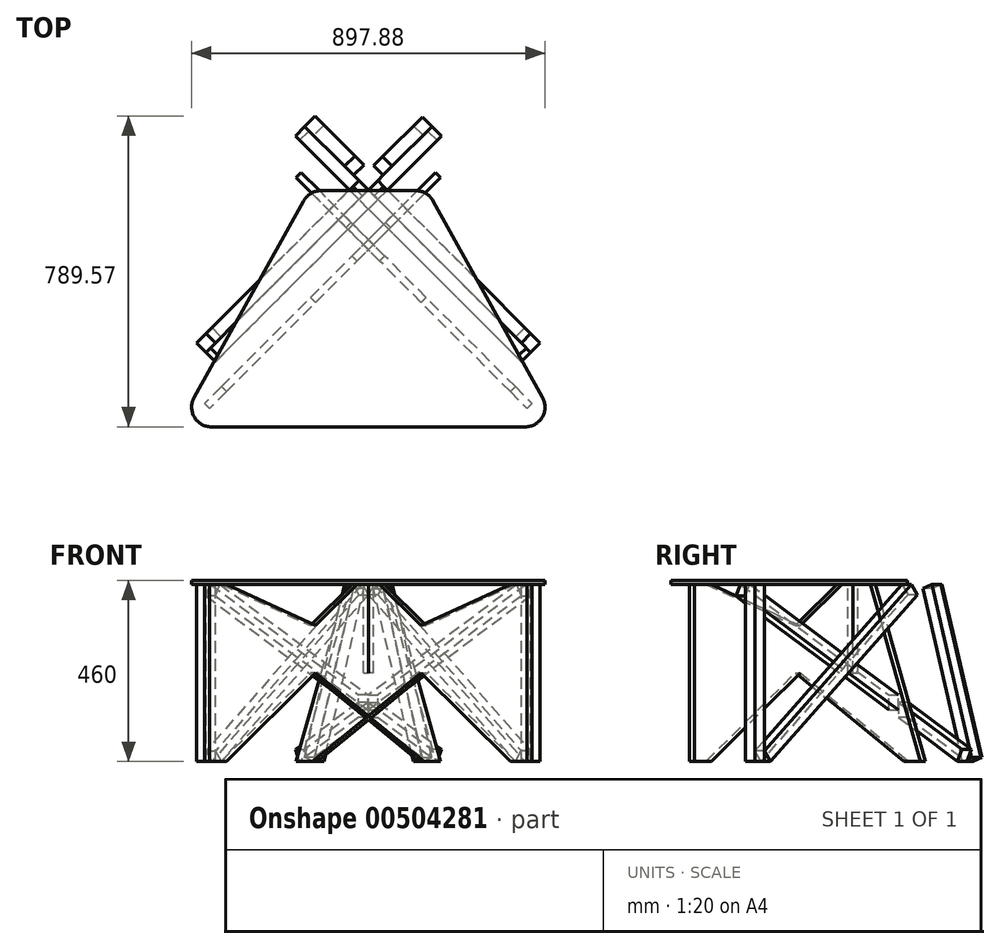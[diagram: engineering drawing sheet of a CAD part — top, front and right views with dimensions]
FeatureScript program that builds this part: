
annotation { "Feature Type Name" : "Feature", "Feature Type Description" : "" }
export const myFeature = defineFeature(function(context is Context, id is Id, definition is map)
    precondition{}
    {
        {
            var Q0;
            Q0=qCreatedBy(makeId("Top.planeOp"),FACE);
            var sketch = newSketch(context, id + "F0", { "sketchPlane" : qUnion([Q0])});
            skLineSegment(sketch, "E0.bottom", {"start": v(450, -300) * mm, "end": v(-450, -300) * mm, "construction": true});
            skLineSegment(sketch, "E0.top", {"start": v(450, 300) * mm, "end": v(-450, 300) * mm, "construction": true});
            skLineSegment(sketch, "E0.left", {"start": v(450, -300) * mm, "end": v(450, 300) * mm, "construction": true});
            skLineSegment(sketch, "E0.right", {"start": v(-450, -300) * mm, "end": v(-450, 300) * mm, "construction": true});
            skPoint(sketch, "E0.middle", {"position": v(0, 0) * mm});
            skLineSegment(sketch, "E1", {"start": v(-450, -250) * mm, "end": v(100, 300) * mm, "construction": true});
            skPoint(sketch, "E2", {"position": v(0, 300) * mm});
            skLineSegment(sketch, "E3.0", {"start": v(-425.96, -274.04) * mm, "end": v(148.08, 300) * mm, "construction": true});
            skLineSegment(sketch, "E4.0", {"start": v(-401.92, -298.08) * mm, "end": v(196.17, 300) * mm, "construction": true});
            skLineSegment(sketch, "E5.MirrorCS", {"start": v(401.92, -298.08) * mm, "end": v(-196.17, 300) * mm, "construction": true});
            skLineSegment(sketch, "E6.MirrorCS", {"start": v(450, -250) * mm, "end": v(-100, 300) * mm, "construction": true});
            skLineSegment(sketch, "E7.MirrorCS", {"start": v(425.96, -274.04) * mm, "end": v(-148.08, 300) * mm, "construction": true});
            skLineSegment(sketch, "E8", {"start": v(-24.04, 127.88) * mm, "end": v(0, 103.83) * mm});
            skLineSegment(sketch, "E9", {"start": v(0, 200) * mm, "end": v(24.04, 175.96) * mm});
            skLineSegment(sketch, "E10", {"start": v(-24.75, 127.88) * mm, "end": v(0, 152.62) * mm});
            skLineSegment(sketch, "E11", {"start": v(0, 152.62) * mm, "end": v(24.75, 127.88) * mm});
            skLineSegment(sketch, "E12", {"start": v(24.75, 127.88) * mm, "end": v(0, 103.13) * mm});
            skLineSegment(sketch, "E13", {"start": v(0, 103.13) * mm, "end": v(-24.75, 127.88) * mm});
            skLineSegment(sketch, "E14", {"start": v(-24.04, 127.88) * mm, "end": v(24.04, 127.88) * mm, "construction": true});
            skLineSegment(sketch, "E15", {"start": v(-164.3, 274.32) * mm, "end": v(-442.63, -225.68) * mm});
            skLineSegment(sketch, "E16", {"start": v(-398.94, -300) * mm, "end": v(398.94, -300) * mm});
            skLineSegment(sketch, "E17", {"start": v(442.63, -225.68) * mm, "end": v(164.3, 274.32) * mm});
            skLineSegment(sketch, "E18", {"start": v(120.6, 300) * mm, "end": v(-120.6, 300) * mm});
            skPoint(sketch, "E19.visualSharp", {"position": v(-484, -300) * mm});
            skArc(sketch, "E19.filletArc", {"start": v(-442.63, -225.68) * mm, "mid": v(-442.05, -275.34) * mm, "end": v(-398.94, -300) * mm});
            skPoint(sketch, "E20.visualSharp", {"position": v(484, -300) * mm});
            skArc(sketch, "E20.filletArc", {"start": v(398.94, -300) * mm, "mid": v(442.05, -275.34) * mm, "end": v(442.63, -225.68) * mm});
            skPoint(sketch, "E21.visualSharp", {"position": v(150, 300) * mm});
            skArc(sketch, "E21.filletArc", {"start": v(164.3, 274.32) * mm, "mid": v(145.95, 293.1) * mm, "end": v(120.6, 300) * mm});
            skPoint(sketch, "E22.visualSharp", {"position": v(-150, 300) * mm});
            skArc(sketch, "E22.filletArc", {"start": v(-120.6, 300) * mm, "mid": v(-145.95, 293.1) * mm, "end": v(-164.3, 274.32) * mm});
            skSolve(sketch);
        }
        {
            var Q0;
            Q0=qCreatedBy(makeId("Right.planeOp"),FACE);
            var sketch = newSketch(context, id + "F1", { "sketchPlane" : qUnion([Q0])});
            skLineSegment(sketch, "E23.bottom", {"start": v(405.9, -225) * mm, "end": v(-405.9, -225) * mm});
            skLineSegment(sketch, "E23.top", {"start": v(405.9, 225) * mm, "end": v(-405.9, 225) * mm});
            skLineSegment(sketch, "E23.left", {"start": v(405.9, -225) * mm, "end": v(405.9, 225) * mm});
            skLineSegment(sketch, "E23.right", {"start": v(-405.91, -225) * mm, "end": v(-405.91, 225) * mm});
            skPoint(sketch, "E23.middle", {"position": v(0, 0) * mm});
            skLineSegment(sketch, "E24.0", {"start": v(-371.91, -225) * mm, "end": v(-371.91, 225) * mm});
            skLineSegment(sketch, "E25", {"start": v(-390.04, 225) * mm, "end": v(405.91, -194.93) * mm});
            skLineSegment(sketch, "E26.0", {"start": v(-405.91, 194.93) * mm, "end": v(390.04, -225) * mm});
            skLineSegment(sketch, "E27", {"start": v(-405.91, 194.93) * mm, "end": v(-390.04, 225) * mm});
            skLineSegment(sketch, "E28", {"start": v(390.04, -225) * mm, "end": v(405.9, -194.93) * mm});
            skLineSegment(sketch, "E29", {"start": v(-397.98, 209.96) * mm, "end": v(397.98, -209.96) * mm, "construction": true});
            skLineSegment(sketch, "E30", {"start": v(-405.9, -85.73) * mm, "end": v(162.5, -85.73) * mm, "construction": true});
            skLineSegment(sketch, "E31", {"start": v(162.5, -85.73) * mm, "end": v(170.42, -70.7) * mm});
            skLineSegment(sketch, "E32", {"start": v(162.5, -85.73) * mm, "end": v(154.56, -100.76) * mm});
            skLineSegment(sketch, "E33", {"start": v(162.49, -85.73) * mm, "end": v(192.56, -101.6) * mm});
            skLineSegment(sketch, "E34", {"start": v(192.56, -101.6) * mm, "end": v(200.5, -86.56) * mm});
            skLineSegment(sketch, "E35", {"start": v(192.56, -101.6) * mm, "end": v(184.63, -116.63) * mm});
            skLineSegment(sketch, "E36", {"start": v(177.53, -93.66) * mm, "end": v(177.53, 225) * mm, "construction": true});
            skLineSegment(sketch, "E37", {"start": v(405.9, -214.47) * mm, "end": v(262.82, 225) * mm});
            skLineSegment(sketch, "E38.0", {"start": v(373.58, -225) * mm, "end": v(230.49, 214.47) * mm});
            skLineSegment(sketch, "E39", {"start": v(262.82, 225) * mm, "end": v(230.49, 214.47) * mm});
            skLineSegment(sketch, "E40", {"start": v(373.58, -225) * mm, "end": v(405.9, -214.47) * mm});
            skLineSegment(sketch, "E41", {"start": v(156.26, 225) * mm, "end": v(-371.9, -198.47) * mm});
            skLineSegment(sketch, "E42.0", {"start": v(177.53, 198.47) * mm, "end": v(-350.64, -225) * mm});
            skLineSegment(sketch, "E43", {"start": v(156.26, 225) * mm, "end": v(177.53, 198.47) * mm});
            skLineSegment(sketch, "E44", {"start": v(-350.64, -225) * mm, "end": v(-371.9, -198.47) * mm});
            skLineSegment(sketch, "E45", {"start": v(177.53, -74.44) * mm, "end": v(135, -52) * mm});
            skLineSegment(sketch, "E46", {"start": v(135, -52) * mm, "end": v(135, -90.44) * mm});
            skLineSegment(sketch, "E47", {"start": v(135, -71.22) * mm, "end": v(162.5, -85.73) * mm});
            skLineSegment(sketch, "E48", {"start": v(177.53, -74.44) * mm, "end": v(177.53, -93.66) * mm});
            skSolve(sketch);
        }
        {
            var Q0;
            {var subQ4=sQuery(id+"F1.wireOp",EDGE,"E23.right");var subQ6=sQuery(id+"F1.wireOp",EDGE,"E23.bottom");var subQ8=makeQuery(id+"F1.imprint","INTERSECT",VERTEX,{"derivedFrom":[subQ6,subQ4]});Q0=makeQuery(id+"F1.imprint","IMPRINT",FACE,{"disambiguationData":[TD([[makeQuery(id+"F1.imprint","IMPRINT",EDGE,{"disambiguationData":[TD([[subQ8,1.0]])],"derivedFrom":subQ6}),-1.0]])]});}
            var Q1;
            {var subQ5=sQuery(id+"F1.wireOp",EDGE,"E27");Q1=makeQuery(id+"F1.imprint","IMPRINT",FACE,{"disambiguationData":[TD([[makeQuery(id+"F1.imprint","IMPRINT",EDGE,{"derivedFrom":subQ5}),-1.0]])]});}
            var Q2;
            {var subQ0=sQuery(id+"F1.wireOp",EDGE,"E24.0");var subQ1=sQuery(id+"F1.wireOp",EDGE,"E23.top");var subQ2=makeQuery(id+"F1.imprint","INTERSECT",VERTEX,{"derivedFrom":[subQ1,subQ0]});Q2=makeQuery(id+"F1.imprint","IMPRINT",FACE,{"disambiguationData":[TD([[makeQuery(id+"F1.imprint","IMPRINT",EDGE,{"disambiguationData":[TD([[subQ2,1.0]])],"derivedFrom":subQ0}),1.0]])]});}
            var Q3;
            {var subQ3=sQuery(id+"F1.wireOp",EDGE,"E27");Q3=makeQuery(id+"F1.imprint","IMPRINT",FACE,{"disambiguationData":[TD([[makeQuery(id+"F1.imprint","IMPRINT",EDGE,{"derivedFrom":subQ3}),1.0]])]});}
            extrude(context, id + "F2", {"entities" : qUnion([Q0, Q1, Q2, Q3]), "depth" : 34 * mm});
        }
        {
            var Q0;
            {var subQ5=sQuery(id+"F1.wireOp",EDGE,"E44");Q0=makeQuery(id+"F1.imprint","IMPRINT",FACE,{"disambiguationData":[TD([[makeQuery(id+"F1.imprint","IMPRINT",EDGE,{"derivedFrom":subQ5}),-1.0]])]});}
            var Q1;
            {var subQ0=sQuery(id+"F1.wireOp",EDGE,"E41");var subQ1=sQuery(id+"F1.wireOp",EDGE,"E25");var subQ2=makeQuery(id+"F1.imprint","INTERSECT",VERTEX,{"derivedFrom":[subQ1,subQ0]});Q1=makeQuery(id+"F1.imprint","IMPRINT",FACE,{"disambiguationData":[TD([[makeQuery(id+"F1.imprint","IMPRINT",EDGE,{"disambiguationData":[TD([[subQ2,-1.0]])],"derivedFrom":subQ1}),-1.0]])]});}
            var Q2;
            {var subQ5=sQuery(id+"F1.wireOp",EDGE,"E43");Q2=makeQuery(id+"F1.imprint","IMPRINT",FACE,{"disambiguationData":[TD([[makeQuery(id+"F1.imprint","IMPRINT",EDGE,{"derivedFrom":subQ5}),-1.0]])]});}
            extrude(context, id + "F3", {"entities" : qUnion([Q0, Q1, Q2]), "depth" : 34 * mm});
        }
        {
            var Q0;
            {var subQ5=sQuery(id+"F1.wireOp",EDGE,"E27");Q0=makeQuery(id+"F1.imprint","IMPRINT",FACE,{"disambiguationData":[TD([[makeQuery(id+"F1.imprint","IMPRINT",EDGE,{"derivedFrom":subQ5}),-1.0]])]});}
            var Q1;
            {var subQ0=sQuery(id+"F1.wireOp",EDGE,"E26.0");var subQ1=sQuery(id+"F1.wireOp",EDGE,"E24.0");var subQ2=makeQuery(id+"F1.imprint","INTERSECT",VERTEX,{"derivedFrom":[subQ1,subQ0]});Q1=makeQuery(id+"F1.imprint","IMPRINT",FACE,{"disambiguationData":[TD([[makeQuery(id+"F1.imprint","IMPRINT",EDGE,{"disambiguationData":[TD([[subQ2,-1.0]])],"derivedFrom":subQ1}),-1.0]])]});}
            var Q2;
            {var subQ0=sQuery(id+"F1.wireOp",EDGE,"E41");var subQ1=sQuery(id+"F1.wireOp",EDGE,"E25");var subQ2=makeQuery(id+"F1.imprint","INTERSECT",VERTEX,{"derivedFrom":[subQ1,subQ0]});Q2=makeQuery(id+"F1.imprint","IMPRINT",FACE,{"disambiguationData":[TD([[makeQuery(id+"F1.imprint","IMPRINT",EDGE,{"disambiguationData":[TD([[subQ2,-1.0]])],"derivedFrom":subQ1}),-1.0]])]});}
            var Q3;
            {var subQ0=sQuery(id+"F1.wireOp",EDGE,"E32");Q3=makeQuery(id+"F1.imprint","IMPRINT",FACE,{"disambiguationData":[TD([[makeQuery(id+"F1.imprint","IMPRINT",EDGE,{"derivedFrom":subQ0}),1.0]])]});}
            var Q4;
            {var subQ4=sQuery(id+"F1.wireOp",EDGE,"E34");Q4=makeQuery(id+"F1.imprint","IMPRINT",FACE,{"disambiguationData":[TD([[makeQuery(id+"F1.imprint","IMPRINT",EDGE,{"derivedFrom":subQ4}),-1.0]])]});}
            var Q5;
            {var subQ5=sQuery(id+"F1.wireOp",EDGE,"E38.0");var subQ6=sQuery(id+"F1.wireOp",EDGE,"E25");var subQ7=makeQuery(id+"F1.imprint","INTERSECT",VERTEX,{"derivedFrom":[subQ6,subQ5]});Q5=makeQuery(id+"F1.imprint","IMPRINT",FACE,{"disambiguationData":[TD([[makeQuery(id+"F1.imprint","IMPRINT",EDGE,{"disambiguationData":[TD([[subQ7,-1.0]])],"derivedFrom":subQ6}),-1.0]])]});}
            var Q6;
            {var subQ1=sQuery(id+"F1.wireOp",EDGE,"E26.0");var subQ3=sQuery(id+"F1.wireOp",EDGE,"E40");var subQ4=makeQuery(id+"F1.imprint","INTERSECT",VERTEX,{"derivedFrom":[subQ1,subQ3]});Q6=makeQuery(id+"F1.imprint","IMPRINT",FACE,{"disambiguationData":[TD([[makeQuery(id+"F1.imprint","IMPRINT",EDGE,{"disambiguationData":[TD([[subQ4,-1.0]])],"derivedFrom":subQ3}),-1.0]])]});}
            var Q7;
            {var subQ1=sQuery(id+"F1.wireOp",EDGE,"E25");var subQ3=sQuery(id+"F1.wireOp",EDGE,"E37");var subQ4=makeQuery(id+"F1.imprint","INTERSECT",VERTEX,{"derivedFrom":[subQ1,subQ3]});Q7=makeQuery(id+"F1.imprint","IMPRINT",FACE,{"disambiguationData":[TD([[makeQuery(id+"F1.imprint","IMPRINT",EDGE,{"disambiguationData":[TD([[subQ4,1.0]])],"derivedFrom":subQ3}),-1.0]])]});}
            var Q8;
            {var subQ0=sQuery(id+"F1.wireOp",EDGE,"E34");Q8=makeQuery(id+"F1.imprint","IMPRINT",FACE,{"disambiguationData":[TD([[makeQuery(id+"F1.imprint","IMPRINT",EDGE,{"derivedFrom":subQ0}),1.0]])]});}
            var Q9;
            {var subQ0=sQuery(id+"F1.wireOp",EDGE,"E32");Q9=makeQuery(id+"F1.imprint","IMPRINT",FACE,{"disambiguationData":[TD([[makeQuery(id+"F1.imprint","IMPRINT",EDGE,{"derivedFrom":subQ0}),-1.0]])]});}
            var Q10;
            {var subQ0=sQuery(id+"F1.wireOp",EDGE,"E46");var subQ6=sQuery(id+"F1.wireOp",EDGE,"E26.0");var subQ8=makeQuery(id+"F1.imprint","INTERSECT",VERTEX,{"derivedFrom":[subQ6,subQ0]});Q10=makeQuery(id+"F1.imprint","IMPRINT",FACE,{"disambiguationData":[TD([[makeQuery(id+"F1.imprint","IMPRINT",EDGE,{"disambiguationData":[TD([[subQ8,1.0]])],"derivedFrom":subQ6}),1.0]])]});}
            var Q11;
            {var subQ0=sQuery(id+"F1.wireOp",EDGE,"E31");Q11=makeQuery(id+"F1.imprint","IMPRINT",FACE,{"disambiguationData":[TD([[makeQuery(id+"F1.imprint","IMPRINT",EDGE,{"derivedFrom":subQ0}),-1.0]])]});}
            var Q12;
            {var subQ0=sQuery(id+"F1.wireOp",EDGE,"E31");Q12=makeQuery(id+"F1.imprint","IMPRINT",FACE,{"disambiguationData":[TD([[makeQuery(id+"F1.imprint","IMPRINT",EDGE,{"derivedFrom":subQ0}),1.0]])]});}
            extrude(context, id + "F4", {"entities" : qUnion([Q0, Q1, Q2, Q3, Q4, Q5, Q6, Q7, Q8, Q9, Q10, Q11, Q12]), "oppositeDirection" : true, "depth" : 34 * mm});
        }
        {
            var Q0;
            {var subQ5=sQuery(id+"F1.wireOp",EDGE,"E39");Q0=makeQuery(id+"F1.imprint","IMPRINT",FACE,{"disambiguationData":[TD([[makeQuery(id+"F1.imprint","IMPRINT",EDGE,{"derivedFrom":subQ5}),1.0]])]});}
            var Q1;
            {var subQ5=sQuery(id+"F1.wireOp",EDGE,"E38.0");var subQ6=sQuery(id+"F1.wireOp",EDGE,"E25");var subQ7=makeQuery(id+"F1.imprint","INTERSECT",VERTEX,{"derivedFrom":[subQ6,subQ5]});Q1=makeQuery(id+"F1.imprint","IMPRINT",FACE,{"disambiguationData":[TD([[makeQuery(id+"F1.imprint","IMPRINT",EDGE,{"disambiguationData":[TD([[subQ7,-1.0]])],"derivedFrom":subQ6}),-1.0]])]});}
            var Q2;
            {var subQ0=sQuery(id+"F1.wireOp",EDGE,"E40");var subQ1=sQuery(id+"F1.wireOp",EDGE,"E28");var subQ2=makeQuery(id+"F1.imprint","INTERSECT",VERTEX,{"derivedFrom":[subQ1,subQ0]});Q2=makeQuery(id+"F1.imprint","IMPRINT",FACE,{"disambiguationData":[TD([[makeQuery(id+"F1.imprint","IMPRINT",EDGE,{"disambiguationData":[TD([[subQ2,-1.0]])],"derivedFrom":subQ1}),-1.0]])]});}
            var Q3;
            {var subQ0=sQuery(id+"F1.wireOp",EDGE,"E38.0");var subQ1=sQuery(id+"F1.wireOp",EDGE,"E26.0");var subQ2=makeQuery(id+"F1.imprint","INTERSECT",VERTEX,{"derivedFrom":[subQ1,subQ0]});Q3=makeQuery(id+"F1.imprint","IMPRINT",FACE,{"disambiguationData":[TD([[makeQuery(id+"F1.imprint","IMPRINT",EDGE,{"disambiguationData":[TD([[subQ2,-1.0]])],"derivedFrom":subQ1}),-1.0]])]});}
            extrude(context, id + "F5", {"entities" : qUnion([Q0, Q1, Q2, Q3]), "depth" : 37 * mm});
        }
        {
            var Q0;
            Q0=makeQuery(id+"F2.opExtrude","SWEPT_BODY",BODY,{"disambiguationData":[OSD([sQuery(id+"F1.wireOp",EDGE,"E23.bottom"),sQuery(id+"F1.wireOp",EDGE,"E23.top"),sQuery(id+"F1.wireOp",EDGE,"E23.right"),sQuery(id+"F1.wireOp",EDGE,"E24.0")])]});
            var Q1;
            Q1=makeQuery(id+"F3.opExtrude","SWEPT_BODY",BODY,{"disambiguationData":[OSD([sQuery(id+"F1.wireOp",EDGE,"E41"),sQuery(id+"F1.wireOp",EDGE,"E42.0"),sQuery(id+"F1.wireOp",EDGE,"E43"),sQuery(id+"F1.wireOp",EDGE,"E44")])]});
            var Q2;
            Q2=makeQuery(id+"F4.opExtrude","SWEPT_BODY",BODY,{"disambiguationData":[OSD([sQuery(id+"F1.wireOp",EDGE,"E25"),sQuery(id+"F1.wireOp",EDGE,"E26.0"),sQuery(id+"F1.wireOp",EDGE,"E27"),sQuery(id+"F1.wireOp",EDGE,"E28"),sQuery(id+"F1.wireOp",EDGE,"E31"),sQuery(id+"F1.wireOp",EDGE,"E33"),sQuery(id+"F1.wireOp",EDGE,"E34")])]});
            var Q3;
            Q3=makeQuery(id+"F5.opExtrude","SWEPT_BODY",BODY,{"disambiguationData":[OSD([sQuery(id+"F1.wireOp",EDGE,"E37"),sQuery(id+"F1.wireOp",EDGE,"E38.0"),sQuery(id+"F1.wireOp",EDGE,"E39"),sQuery(id+"F1.wireOp",EDGE,"E40")])]});
            var Q4;
            Q4=sQuery(id+"F1.wireOp",EDGE,"E36");
            transform(context, id + "F6", {"entities" : qUnion([Q0, Q1, Q2, Q3]), "transformType" : TransformType.ROTATION, "transformAxis" : qUnion([Q4]), "angle" : 45 * degree, "makeCopy" : false});
        }
        {
            var Q0;
            {var subQ0=sQuery(id+"F1.wireOp",EDGE,"E41");var subQ1=sQuery(id+"F1.wireOp",EDGE,"E25");var subQ2=makeQuery(id+"F1.imprint","INTERSECT",VERTEX,{"derivedFrom":[subQ1,subQ0]});Q0=makeQuery(id+"F1.imprint","IMPRINT",FACE,{"disambiguationData":[TD([[makeQuery(id+"F1.imprint","IMPRINT",EDGE,{"disambiguationData":[TD([[subQ2,-1.0]])],"derivedFrom":subQ1}),-1.0]])]});}
            var Q1;
            {var subQ0=sQuery(id+"F1.wireOp",EDGE,"E26.0");var subQ1=sQuery(id+"F1.wireOp",EDGE,"E24.0");var subQ2=makeQuery(id+"F1.imprint","INTERSECT",VERTEX,{"derivedFrom":[subQ1,subQ0]});Q1=makeQuery(id+"F1.imprint","IMPRINT",FACE,{"disambiguationData":[TD([[makeQuery(id+"F1.imprint","IMPRINT",EDGE,{"disambiguationData":[TD([[subQ2,-1.0]])],"derivedFrom":subQ1}),-1.0]])]});}
            var Q2;
            {var subQ4=sQuery(id+"F1.wireOp",EDGE,"E34");Q2=makeQuery(id+"F1.imprint","IMPRINT",FACE,{"disambiguationData":[TD([[makeQuery(id+"F1.imprint","IMPRINT",EDGE,{"derivedFrom":subQ4}),-1.0]])]});}
            var Q3;
            {var subQ5=sQuery(id+"F1.wireOp",EDGE,"E38.0");var subQ6=sQuery(id+"F1.wireOp",EDGE,"E25");var subQ7=makeQuery(id+"F1.imprint","INTERSECT",VERTEX,{"derivedFrom":[subQ6,subQ5]});Q3=makeQuery(id+"F1.imprint","IMPRINT",FACE,{"disambiguationData":[TD([[makeQuery(id+"F1.imprint","IMPRINT",EDGE,{"disambiguationData":[TD([[subQ7,-1.0]])],"derivedFrom":subQ6}),-1.0]])]});}
            var Q4;
            {var subQ5=sQuery(id+"F1.wireOp",EDGE,"E27");Q4=makeQuery(id+"F1.imprint","IMPRINT",FACE,{"disambiguationData":[TD([[makeQuery(id+"F1.imprint","IMPRINT",EDGE,{"derivedFrom":subQ5}),-1.0]])]});}
            var Q5;
            {var subQ1=sQuery(id+"F1.wireOp",EDGE,"E25");var subQ3=sQuery(id+"F1.wireOp",EDGE,"E37");var subQ4=makeQuery(id+"F1.imprint","INTERSECT",VERTEX,{"derivedFrom":[subQ1,subQ3]});Q5=makeQuery(id+"F1.imprint","IMPRINT",FACE,{"disambiguationData":[TD([[makeQuery(id+"F1.imprint","IMPRINT",EDGE,{"disambiguationData":[TD([[subQ4,1.0]])],"derivedFrom":subQ3}),-1.0]])]});}
            var Q6;
            {var subQ1=sQuery(id+"F1.wireOp",EDGE,"E26.0");var subQ3=sQuery(id+"F1.wireOp",EDGE,"E40");var subQ4=makeQuery(id+"F1.imprint","INTERSECT",VERTEX,{"derivedFrom":[subQ1,subQ3]});Q6=makeQuery(id+"F1.imprint","IMPRINT",FACE,{"disambiguationData":[TD([[makeQuery(id+"F1.imprint","IMPRINT",EDGE,{"disambiguationData":[TD([[subQ4,-1.0]])],"derivedFrom":subQ3}),-1.0]])]});}
            var Q7;
            {var subQ0=sQuery(id+"F1.wireOp",EDGE,"E46");var subQ6=sQuery(id+"F1.wireOp",EDGE,"E26.0");var subQ8=makeQuery(id+"F1.imprint","INTERSECT",VERTEX,{"derivedFrom":[subQ6,subQ0]});Q7=makeQuery(id+"F1.imprint","IMPRINT",FACE,{"disambiguationData":[TD([[makeQuery(id+"F1.imprint","IMPRINT",EDGE,{"disambiguationData":[TD([[subQ8,1.0]])],"derivedFrom":subQ6}),1.0]])]});}
            var Q8;
            {var subQ0=sQuery(id+"F1.wireOp",EDGE,"E34");Q8=makeQuery(id+"F1.imprint","IMPRINT",FACE,{"disambiguationData":[TD([[makeQuery(id+"F1.imprint","IMPRINT",EDGE,{"derivedFrom":subQ0}),1.0]])]});}
            var Q9;
            {var subQ0=sQuery(id+"F1.wireOp",EDGE,"E31");Q9=makeQuery(id+"F1.imprint","IMPRINT",FACE,{"disambiguationData":[TD([[makeQuery(id+"F1.imprint","IMPRINT",EDGE,{"derivedFrom":subQ0}),1.0]])]});}
            var Q10;
            {var subQ0=sQuery(id+"F1.wireOp",EDGE,"E31");Q10=makeQuery(id+"F1.imprint","IMPRINT",FACE,{"disambiguationData":[TD([[makeQuery(id+"F1.imprint","IMPRINT",EDGE,{"derivedFrom":subQ0}),-1.0]])]});}
            var Q11;
            {var subQ3=sQuery(id+"F1.wireOp",EDGE,"E32");Q11=makeQuery(id+"F1.imprint","IMPRINT",FACE,{"disambiguationData":[TD([[makeQuery(id+"F1.imprint","IMPRINT",EDGE,{"derivedFrom":subQ3}),1.0]])]});}
            var Q12;
            {var subQ0=sQuery(id+"F1.wireOp",EDGE,"E32");Q12=makeQuery(id+"F1.imprint","IMPRINT",FACE,{"disambiguationData":[TD([[makeQuery(id+"F1.imprint","IMPRINT",EDGE,{"derivedFrom":subQ0}),-1.0]])]});}
            extrude(context, id + "F7", {"entities" : qUnion([Q0, Q1, Q2, Q3, Q4, Q5, Q6, Q7, Q8, Q9, Q10, Q11, Q12]), "depth" : 34 * mm});
        }
        {
            var Q0;
            {var subQ5=sQuery(id+"F1.wireOp",EDGE,"E44");Q0=makeQuery(id+"F1.imprint","IMPRINT",FACE,{"disambiguationData":[TD([[makeQuery(id+"F1.imprint","IMPRINT",EDGE,{"derivedFrom":subQ5}),-1.0]])]});}
            var Q1;
            {var subQ0=sQuery(id+"F1.wireOp",EDGE,"E41");var subQ1=sQuery(id+"F1.wireOp",EDGE,"E25");var subQ2=makeQuery(id+"F1.imprint","INTERSECT",VERTEX,{"derivedFrom":[subQ1,subQ0]});Q1=makeQuery(id+"F1.imprint","IMPRINT",FACE,{"disambiguationData":[TD([[makeQuery(id+"F1.imprint","IMPRINT",EDGE,{"disambiguationData":[TD([[subQ2,-1.0]])],"derivedFrom":subQ1}),-1.0]])]});}
            var Q2;
            {var subQ5=sQuery(id+"F1.wireOp",EDGE,"E43");Q2=makeQuery(id+"F1.imprint","IMPRINT",FACE,{"disambiguationData":[TD([[makeQuery(id+"F1.imprint","IMPRINT",EDGE,{"derivedFrom":subQ5}),-1.0]])]});}
            extrude(context, id + "F8", {"entities" : qUnion([Q0, Q1, Q2]), "oppositeDirection" : true, "depth" : 34 * mm});
        }
        {
            var Q0;
            {var subQ4=sQuery(id+"F1.wireOp",EDGE,"E23.right");var subQ6=sQuery(id+"F1.wireOp",EDGE,"E23.bottom");var subQ8=makeQuery(id+"F1.imprint","INTERSECT",VERTEX,{"derivedFrom":[subQ6,subQ4]});Q0=makeQuery(id+"F1.imprint","IMPRINT",FACE,{"disambiguationData":[TD([[makeQuery(id+"F1.imprint","IMPRINT",EDGE,{"disambiguationData":[TD([[subQ8,1.0]])],"derivedFrom":subQ6}),-1.0]])]});}
            var Q1;
            {var subQ5=sQuery(id+"F1.wireOp",EDGE,"E27");Q1=makeQuery(id+"F1.imprint","IMPRINT",FACE,{"disambiguationData":[TD([[makeQuery(id+"F1.imprint","IMPRINT",EDGE,{"derivedFrom":subQ5}),-1.0]])]});}
            var Q2;
            {var subQ3=sQuery(id+"F1.wireOp",EDGE,"E27");Q2=makeQuery(id+"F1.imprint","IMPRINT",FACE,{"disambiguationData":[TD([[makeQuery(id+"F1.imprint","IMPRINT",EDGE,{"derivedFrom":subQ3}),1.0]])]});}
            var Q3;
            {var subQ0=sQuery(id+"F1.wireOp",EDGE,"E24.0");var subQ1=sQuery(id+"F1.wireOp",EDGE,"E23.top");var subQ2=makeQuery(id+"F1.imprint","INTERSECT",VERTEX,{"derivedFrom":[subQ1,subQ0]});Q3=makeQuery(id+"F1.imprint","IMPRINT",FACE,{"disambiguationData":[TD([[makeQuery(id+"F1.imprint","IMPRINT",EDGE,{"disambiguationData":[TD([[subQ2,1.0]])],"derivedFrom":subQ0}),1.0]])]});}
            extrude(context, id + "F9", {"entities" : qUnion([Q0, Q1, Q2, Q3]), "oppositeDirection" : true, "depth" : 34 * mm});
        }
        {
            var Q0;
            {var subQ5=sQuery(id+"F1.wireOp",EDGE,"E39");Q0=makeQuery(id+"F1.imprint","IMPRINT",FACE,{"disambiguationData":[TD([[makeQuery(id+"F1.imprint","IMPRINT",EDGE,{"derivedFrom":subQ5}),1.0]])]});}
            var Q1;
            {var subQ5=sQuery(id+"F1.wireOp",EDGE,"E38.0");var subQ6=sQuery(id+"F1.wireOp",EDGE,"E25");var subQ7=makeQuery(id+"F1.imprint","INTERSECT",VERTEX,{"derivedFrom":[subQ6,subQ5]});Q1=makeQuery(id+"F1.imprint","IMPRINT",FACE,{"disambiguationData":[TD([[makeQuery(id+"F1.imprint","IMPRINT",EDGE,{"disambiguationData":[TD([[subQ7,-1.0]])],"derivedFrom":subQ6}),-1.0]])]});}
            var Q2;
            {var subQ0=sQuery(id+"F1.wireOp",EDGE,"E40");var subQ1=sQuery(id+"F1.wireOp",EDGE,"E28");var subQ2=makeQuery(id+"F1.imprint","INTERSECT",VERTEX,{"derivedFrom":[subQ1,subQ0]});Q2=makeQuery(id+"F1.imprint","IMPRINT",FACE,{"disambiguationData":[TD([[makeQuery(id+"F1.imprint","IMPRINT",EDGE,{"disambiguationData":[TD([[subQ2,-1.0]])],"derivedFrom":subQ1}),-1.0]])]});}
            var Q3;
            {var subQ0=sQuery(id+"F1.wireOp",EDGE,"E38.0");var subQ1=sQuery(id+"F1.wireOp",EDGE,"E26.0");var subQ2=makeQuery(id+"F1.imprint","INTERSECT",VERTEX,{"derivedFrom":[subQ1,subQ0]});Q3=makeQuery(id+"F1.imprint","IMPRINT",FACE,{"disambiguationData":[TD([[makeQuery(id+"F1.imprint","IMPRINT",EDGE,{"disambiguationData":[TD([[subQ2,-1.0]])],"derivedFrom":subQ1}),-1.0]])]});}
            extrude(context, id + "F10", {"entities" : qUnion([Q0, Q1, Q2, Q3]), "oppositeDirection" : true, "depth" : 34 * mm});
        }
        {
            var Q0;
            Q0=makeQuery(id+"F7.opExtrude","SWEPT_BODY",BODY,{"disambiguationData":[OSD([sQuery(id+"F1.wireOp",EDGE,"E25"),sQuery(id+"F1.wireOp",EDGE,"E26.0"),sQuery(id+"F1.wireOp",EDGE,"E27"),sQuery(id+"F1.wireOp",EDGE,"E28"),sQuery(id+"F1.wireOp",EDGE,"E32"),sQuery(id+"F1.wireOp",EDGE,"E33"),sQuery(id+"F1.wireOp",EDGE,"E35")])]});
            var Q1;
            Q1=makeQuery(id+"F8.opExtrude","SWEPT_BODY",BODY,{"disambiguationData":[OSD([sQuery(id+"F1.wireOp",EDGE,"E41"),sQuery(id+"F1.wireOp",EDGE,"E42.0"),sQuery(id+"F1.wireOp",EDGE,"E43"),sQuery(id+"F1.wireOp",EDGE,"E44")])]});
            var Q2;
            Q2=makeQuery(id+"F9.opExtrude","SWEPT_BODY",BODY,{"disambiguationData":[OSD([sQuery(id+"F1.wireOp",EDGE,"E23.bottom"),sQuery(id+"F1.wireOp",EDGE,"E23.top"),sQuery(id+"F1.wireOp",EDGE,"E23.right"),sQuery(id+"F1.wireOp",EDGE,"E24.0")])]});
            var Q3;
            Q3=makeQuery(id+"F10.opExtrude","SWEPT_BODY",BODY,{"disambiguationData":[OSD([sQuery(id+"F1.wireOp",EDGE,"E37"),sQuery(id+"F1.wireOp",EDGE,"E38.0"),sQuery(id+"F1.wireOp",EDGE,"E39"),sQuery(id+"F1.wireOp",EDGE,"E40")])]});
            var Q4;
            Q4=sQuery(id+"F1.wireOp",EDGE,"E36");
            transform(context, id + "F11", {"entities" : qUnion([Q0, Q1, Q2, Q3]), "transformType" : TransformType.ROTATION, "transformAxis" : qUnion([Q4]), "angle" : 45 * degree, "oppositeDirection" : true, "makeCopy" : false});
        }
        {
            var Q0;
            Q0=makeQuery(id+"F2.opExtrude","SWEPT_BODY",BODY,{"disambiguationData":[OSD([sQuery(id+"F1.wireOp",EDGE,"E23.bottom"),sQuery(id+"F1.wireOp",EDGE,"E23.top"),sQuery(id+"F1.wireOp",EDGE,"E23.right"),sQuery(id+"F1.wireOp",EDGE,"E24.0")])]});
            var Q1;
            Q1=makeQuery(id+"F3.opExtrude","SWEPT_BODY",BODY,{"disambiguationData":[OSD([sQuery(id+"F1.wireOp",EDGE,"E41"),sQuery(id+"F1.wireOp",EDGE,"E42.0"),sQuery(id+"F1.wireOp",EDGE,"E43"),sQuery(id+"F1.wireOp",EDGE,"E44")])]});
            var Q2;
            Q2=makeQuery(id+"F4.opExtrude","SWEPT_BODY",BODY,{"disambiguationData":[OSD([sQuery(id+"F1.wireOp",EDGE,"E25"),sQuery(id+"F1.wireOp",EDGE,"E26.0"),sQuery(id+"F1.wireOp",EDGE,"E27"),sQuery(id+"F1.wireOp",EDGE,"E28"),sQuery(id+"F1.wireOp",EDGE,"E45")])]});
            var Q3;
            Q3=makeQuery(id+"F5.opExtrude","SWEPT_BODY",BODY,{"disambiguationData":[OSD([sQuery(id+"F1.wireOp",EDGE,"E37"),sQuery(id+"F1.wireOp",EDGE,"E38.0"),sQuery(id+"F1.wireOp",EDGE,"E39"),sQuery(id+"F1.wireOp",EDGE,"E40")])]});
            var Q4;
            Q4=makeQuery(id+"F7.opExtrude","SWEPT_BODY",BODY,{"disambiguationData":[OSD([sQuery(id+"F1.wireOp",EDGE,"E25"),sQuery(id+"F1.wireOp",EDGE,"E26.0"),sQuery(id+"F1.wireOp",EDGE,"E27"),sQuery(id+"F1.wireOp",EDGE,"E28"),sQuery(id+"F1.wireOp",EDGE,"E45")])]});
            var Q5;
            Q5=makeQuery(id+"F8.opExtrude","SWEPT_BODY",BODY,{"disambiguationData":[OSD([sQuery(id+"F1.wireOp",EDGE,"E41"),sQuery(id+"F1.wireOp",EDGE,"E42.0"),sQuery(id+"F1.wireOp",EDGE,"E43"),sQuery(id+"F1.wireOp",EDGE,"E44")])]});
            var Q6;
            Q6=makeQuery(id+"F9.opExtrude","SWEPT_BODY",BODY,{"disambiguationData":[OSD([sQuery(id+"F1.wireOp",EDGE,"E23.bottom"),sQuery(id+"F1.wireOp",EDGE,"E23.top"),sQuery(id+"F1.wireOp",EDGE,"E23.right"),sQuery(id+"F1.wireOp",EDGE,"E24.0")])]});
            var Q7;
            Q7=makeQuery(id+"F10.opExtrude","SWEPT_BODY",BODY,{"disambiguationData":[OSD([sQuery(id+"F1.wireOp",EDGE,"E37"),sQuery(id+"F1.wireOp",EDGE,"E38.0"),sQuery(id+"F1.wireOp",EDGE,"E39"),sQuery(id+"F1.wireOp",EDGE,"E40")])]});
            transform(context, id + "F12", {"entities" : qUnion([Q0, Q1, Q2, Q3, Q4, Q5, Q6, Q7]), "transformType" : TransformType.TRANSLATION_3D, "dx" : 0 * mm, "dy" : -25.6 * mm, "dz" : 0 * mm, "makeCopy" : false});
        }
        {
            var Q0;
            Q0=makeQuery(id+"F0.imprint","IMPRINT",FACE,{"disambiguationData":[TD([[makeQuery(id+"F0.imprint","IMPRINT",EDGE,{"derivedFrom":sQuery(id+"F0.wireOp",EDGE,"E10")}),-1.0]])]});
            extrude(context, id + "F13", {"entities" : qUnion([Q0]), "operationType" : NewBodyOperationType.REMOVE, "oppositeDirection" : true, "depth" : 85 * mm});
        }
        {
            var Q0;
            Q0=makeQuery(id+"F0.imprint","IMPRINT",FACE,{"disambiguationData":[TD([[makeQuery(id+"F0.imprint","IMPRINT",EDGE,{"derivedFrom":sQuery(id+"F0.wireOp",EDGE,"E10")}),-1.0]])]});
            extrude(context, id + "F14", {"entities" : qUnion([Q0]), "operationType" : NewBodyOperationType.REMOVE, "oppositeDirection" : true, "depth" : 150 * mm, "hasSecondDirection" : true, "secondDirectionOppositeDirection" : true, "secondDirectionDepth" : 84 * mm});
        }
        {
            var Q0;
            Q0=makeQuery(id+"F0.imprint","IMPRINT",FACE,{"disambiguationData":[TD([[makeQuery(id+"F0.imprint","IMPRINT",EDGE,{"derivedFrom":sQuery(id+"F0.wireOp",EDGE,"E10")}),1.0]])]});
            var Q1;
            Q1=makeQuery(id+"F0.imprint","IMPRINT",FACE,{"disambiguationData":[TD([[makeQuery(id+"F0.imprint","IMPRINT",EDGE,{"derivedFrom":sQuery(id+"F0.wireOp",EDGE,"E10")}),-1.0]])]});
            extrude(context, id + "F15", {"entities" : qUnion([Q0, Q1]), "depth" : 235 * mm, "hasSecondDirection" : true, "secondDirectionOppositeDirection" : false, "secondDirectionDepth" : 225 * mm});
        }
        {
            var Q0;
            Q0=qCreatedBy(makeId("Top.planeOp"),FACE);
            var sketch = newSketch(context, id + "F16", { "sketchPlane" : qUnion([Q0])});
            skLineSegment(sketch, "E49.right", {"start": v(-475.01, -198.82) * mm, "end": v(-475.01, 251.18) * mm});
            skPoint(sketch, "E49.middle", {"position": v(-69.1, 26.18) * mm});
            skLineSegment(sketch, "E50", {"start": v(-475.01, 26.18) * mm, "end": v(94.99, 26.18) * mm, "construction": true});
            skLineSegment(sketch, "E51", {"start": v(-415.01, 251.18) * mm, "end": v(-95.01, 146.18) * mm});
            skLineSegment(sketch, "E52", {"start": v(-95.01, 146.18) * mm, "end": v(54.99, 251.18) * mm});
            skLineSegment(sketch, "E53", {"start": v(-415.01, 251.18) * mm, "end": v(-475.01, 251.18) * mm});
            skLineSegment(sketch, "E54", {"start": v(-475.01, -198.82) * mm, "end": v(-415.01, -198.82) * mm});
            skLineSegment(sketch, "E55", {"start": v(54.99, 251.18) * mm, "end": v(174.99, 251.18) * mm});
            skLineSegment(sketch, "E56", {"start": v(-95.01, 26.18) * mm, "end": v(294.99, -198.82) * mm});
            skLineSegment(sketch, "E57", {"start": v(174.99, 251.18) * mm, "end": v(354.99, -198.82) * mm});
            skLineSegment(sketch, "E58", {"start": v(-415.01, -198.82) * mm, "end": v(-95.01, 26.18) * mm});
            skLineSegment(sketch, "E59", {"start": v(94.99, 26.18) * mm, "end": v(94.99, 251.18) * mm});
            skLineSegment(sketch, "E60", {"start": v(294.99, -198.82) * mm, "end": v(354.99, -198.82) * mm});
            skLineSegment(sketch, "E61", {"start": v(94.99, 26.18) * mm, "end": v(112.99, 26.18) * mm});
            skLineSegment(sketch, "E62", {"start": v(112.99, 26.18) * mm, "end": v(112.99, 251.18) * mm});
            skSolve(sketch);
        }
        {
            var Q0;
            Q0=makeQuery(id+"F16.imprint","IMPRINT",FACE,{"disambiguationData":[TD([[makeQuery(id+"F16.imprint","IMPRINT",EDGE,{"derivedFrom":sQuery(id+"F16.wireOp",EDGE,"E49.right")}),-1.0]])]});
            extrude(context, id + "F17", {"entities" : qUnion([Q0]), "depth" : 18 * mm, "offsetDistance" : 25 * mm});
        }
        {
            var Q0;
            Q0=makeQuery(id+"F17.opExtrude","SWEPT_BODY",BODY,{"disambiguationData":[OSD([sQuery(id+"F16.wireOp",EDGE,"E49.right"),sQuery(id+"F16.wireOp",EDGE,"E51"),sQuery(id+"F16.wireOp",EDGE,"E52"),sQuery(id+"F16.wireOp",EDGE,"E53"),sQuery(id+"F16.wireOp",EDGE,"E54"),sQuery(id+"F16.wireOp",EDGE,"E55"),sQuery(id+"F16.wireOp",EDGE,"E56"),sQuery(id+"F16.wireOp",EDGE,"E57"),sQuery(id+"F16.wireOp",EDGE,"E58"),sQuery(id+"F16.wireOp",EDGE,"E59"),sQuery(id+"F16.wireOp",EDGE,"E60"),sQuery(id+"F16.wireOp",EDGE,"E61"),sQuery(id+"F16.wireOp",EDGE,"E62")])]});
            var Q1;
            Q1=makeQuery(id+"F17.opExtrude","CAP_EDGE",EDGE,{"disambiguationData":[OSD([sQuery(id+"F16.wireOp",EDGE,"E61")])],"isStart":false});
            transform(context, id + "F18", {"entities" : qUnion([Q0]), "transformType" : TransformType.ROTATION, "transformAxis" : qUnion([Q1]), "angle" : 90 * degree, "makeCopy" : false});
        }
        {
            var Q0;
            Q0=makeQuery(id+"F17.opExtrude","SWEPT_BODY",BODY,{"disambiguationData":[OSD([sQuery(id+"F16.wireOp",EDGE,"E49.right"),sQuery(id+"F16.wireOp",EDGE,"E51"),sQuery(id+"F16.wireOp",EDGE,"E52"),sQuery(id+"F16.wireOp",EDGE,"E53"),sQuery(id+"F16.wireOp",EDGE,"E54"),sQuery(id+"F16.wireOp",EDGE,"E55"),sQuery(id+"F16.wireOp",EDGE,"E56"),sQuery(id+"F16.wireOp",EDGE,"E57"),sQuery(id+"F16.wireOp",EDGE,"E58"),sQuery(id+"F16.wireOp",EDGE,"E59"),sQuery(id+"F16.wireOp",EDGE,"E60"),sQuery(id+"F16.wireOp",EDGE,"E61"),sQuery(id+"F16.wireOp",EDGE,"E62")])]});
            var Q1;
            Q1=makeQuery(id+"F17.opExtrude","CAP_EDGE",EDGE,{"disambiguationData":[OSD([sQuery(id+"F16.wireOp",EDGE,"E59")])],"isStart":true});
            transform(context, id + "F19", {"entities" : qUnion([Q0]), "transformType" : TransformType.ROTATION, "transformAxis" : qUnion([Q1]), "angle" : 45 * degree, "makeCopy" : false});
        }
        {
            var Q0;
            Q0=makeQuery(id+"F17.opExtrude","SWEPT_BODY",BODY,{"disambiguationData":[OSD([sQuery(id+"F16.wireOp",EDGE,"E49.right"),sQuery(id+"F16.wireOp",EDGE,"E51"),sQuery(id+"F16.wireOp",EDGE,"E52"),sQuery(id+"F16.wireOp",EDGE,"E53"),sQuery(id+"F16.wireOp",EDGE,"E54"),sQuery(id+"F16.wireOp",EDGE,"E55"),sQuery(id+"F16.wireOp",EDGE,"E56"),sQuery(id+"F16.wireOp",EDGE,"E57"),sQuery(id+"F16.wireOp",EDGE,"E58"),sQuery(id+"F16.wireOp",EDGE,"E59"),sQuery(id+"F16.wireOp",EDGE,"E60"),sQuery(id+"F16.wireOp",EDGE,"E61"),sQuery(id+"F16.wireOp",EDGE,"E62")])]});
            var Q1;
            Q1=qCreatedBy(makeId("Origin.pointOp"),VERTEX);
            var Q2;
            Q2=makeQuery(id+"F17.opExtrude","CAP_VERTEX",VERTEX,{"disambiguationData":[OSD([sQuery(id+"F16.wireOp",EDGE,"E59"),sQuery(id+"F16.wireOp",EDGE,"E61")])],"isStart":false});
            transform(context, id + "F20", {"entities" : qUnion([Q0]), "transformType" : TransformType.TRANSLATION_ENTITY, "oppositeDirectionEntity" : true, "transformLine" : qUnion([Q1, Q2]), "makeCopy" : false});
        }
        {
            var Q0;
            Q0=makeQuery(id+"F17.opExtrude","SWEPT_BODY",BODY,{"disambiguationData":[OSD([sQuery(id+"F16.wireOp",EDGE,"E49.right"),sQuery(id+"F16.wireOp",EDGE,"E51"),sQuery(id+"F16.wireOp",EDGE,"E52"),sQuery(id+"F16.wireOp",EDGE,"E53"),sQuery(id+"F16.wireOp",EDGE,"E54"),sQuery(id+"F16.wireOp",EDGE,"E55"),sQuery(id+"F16.wireOp",EDGE,"E56"),sQuery(id+"F16.wireOp",EDGE,"E57"),sQuery(id+"F16.wireOp",EDGE,"E58"),sQuery(id+"F16.wireOp",EDGE,"E59"),sQuery(id+"F16.wireOp",EDGE,"E60"),sQuery(id+"F16.wireOp",EDGE,"E61"),sQuery(id+"F16.wireOp",EDGE,"E62")])]});
            var Q1;
            Q1=qCreatedBy(makeId("Right.planeOp"),FACE);
            mirror(context, id + "F21", {"entities" : qUnion([Q0]), "mirrorPlane" : qUnion([Q1])});
        }
        {
            var Q0;
            Q0=makeQuery(id+"F15.opExtrude","SWEPT_BODY",BODY,{"disambiguationData":[OSD([sQuery(id+"F0.wireOp",EDGE,"E15"),sQuery(id+"F0.wireOp",EDGE,"E16"),sQuery(id+"F0.wireOp",EDGE,"E17"),sQuery(id+"F0.wireOp",EDGE,"E18"),sQuery(id+"F0.wireOp",EDGE,"E19.filletArc"),sQuery(id+"F0.wireOp",EDGE,"E20.filletArc"),sQuery(id+"F0.wireOp",EDGE,"E21.filletArc"),sQuery(id+"F0.wireOp",EDGE,"E22.filletArc")])]});
            var Q1;
            Q1=makeQuery(id+"F15.opExtrude","SWEPT_FACE",FACE,{"disambiguationData":[OSD([sQuery(id+"F0.wireOp",EDGE,"E16")])]});
            transform(context, id + "F22", {"entities" : qUnion([Q0]), "transformType" : TransformType.TRANSLATION_DISTANCE, "transformDirection" : qUnion([Q1]), "distance" : 150 * mm, "makeCopy" : false});
        }
    });
